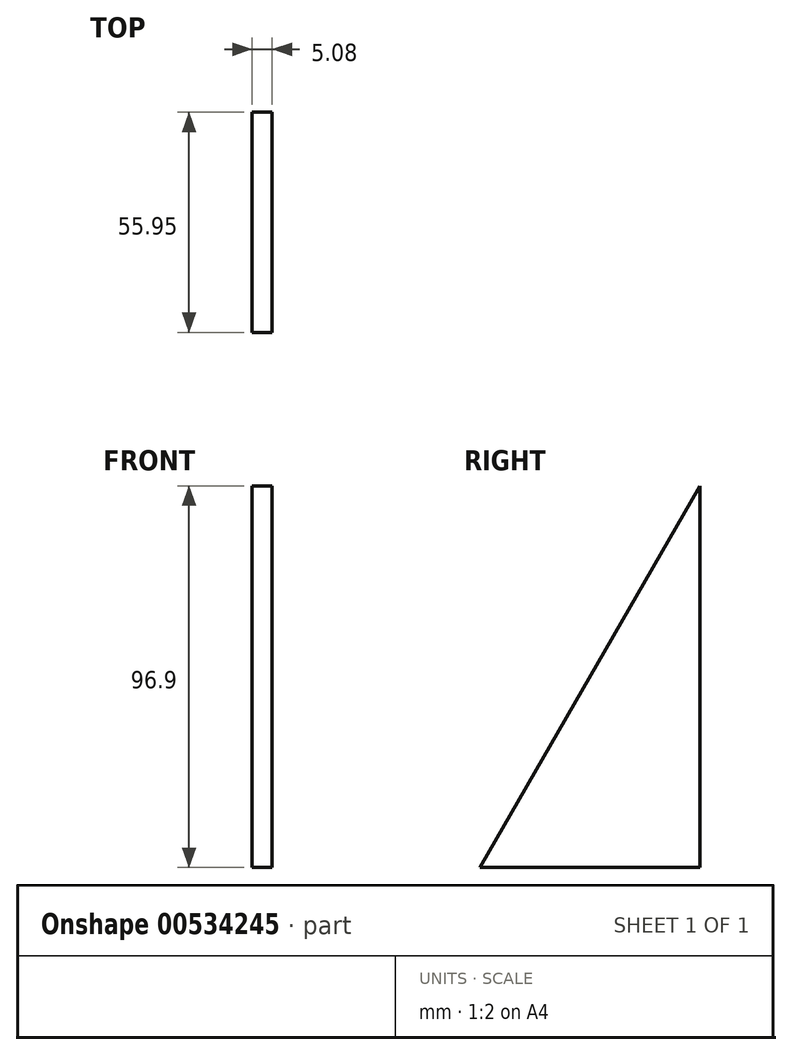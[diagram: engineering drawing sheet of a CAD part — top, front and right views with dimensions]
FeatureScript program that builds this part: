
annotation { "Feature Type Name" : "Feature", "Feature Type Description" : "" }
export const myFeature = defineFeature(function(context is Context, id is Id, definition is map)
    precondition{}
    {
        {
            var Q0;
            Q0=qCreatedBy(makeId("Right.planeOp"),FACE);
            var sketch = newSketch(context, id + "F0", { "sketchPlane" : qUnion([Q0])});
            skLineSegment(sketch, "E0", {"start": v(0, 96.9) * mm, "end": v(0, 0) * mm});
            skLineSegment(sketch, "E1", {"start": v(0, 0) * mm, "end": v(-55.95, 0) * mm});
            skLineSegment(sketch, "E2", {"start": v(-55.95, 0) * mm, "end": v(0, 96.9) * mm});
            skSolve(sketch);
        }
        {
            var Q0;
            Q0=makeQuery(id+"F0.imprint","IMPRINT",FACE,{"disambiguationData":[TD([[makeQuery(id+"F0.imprint","IMPRINT",EDGE,{"derivedFrom":sQuery(id+"F0.wireOp",EDGE,"E0")}),-1.0]])]});
            extrude(context, id + "F1", {"entities" : qUnion([Q0]), "depth" : 5.08 * mm, "offsetDistance" : 25.4 * mm});
        }
    });
